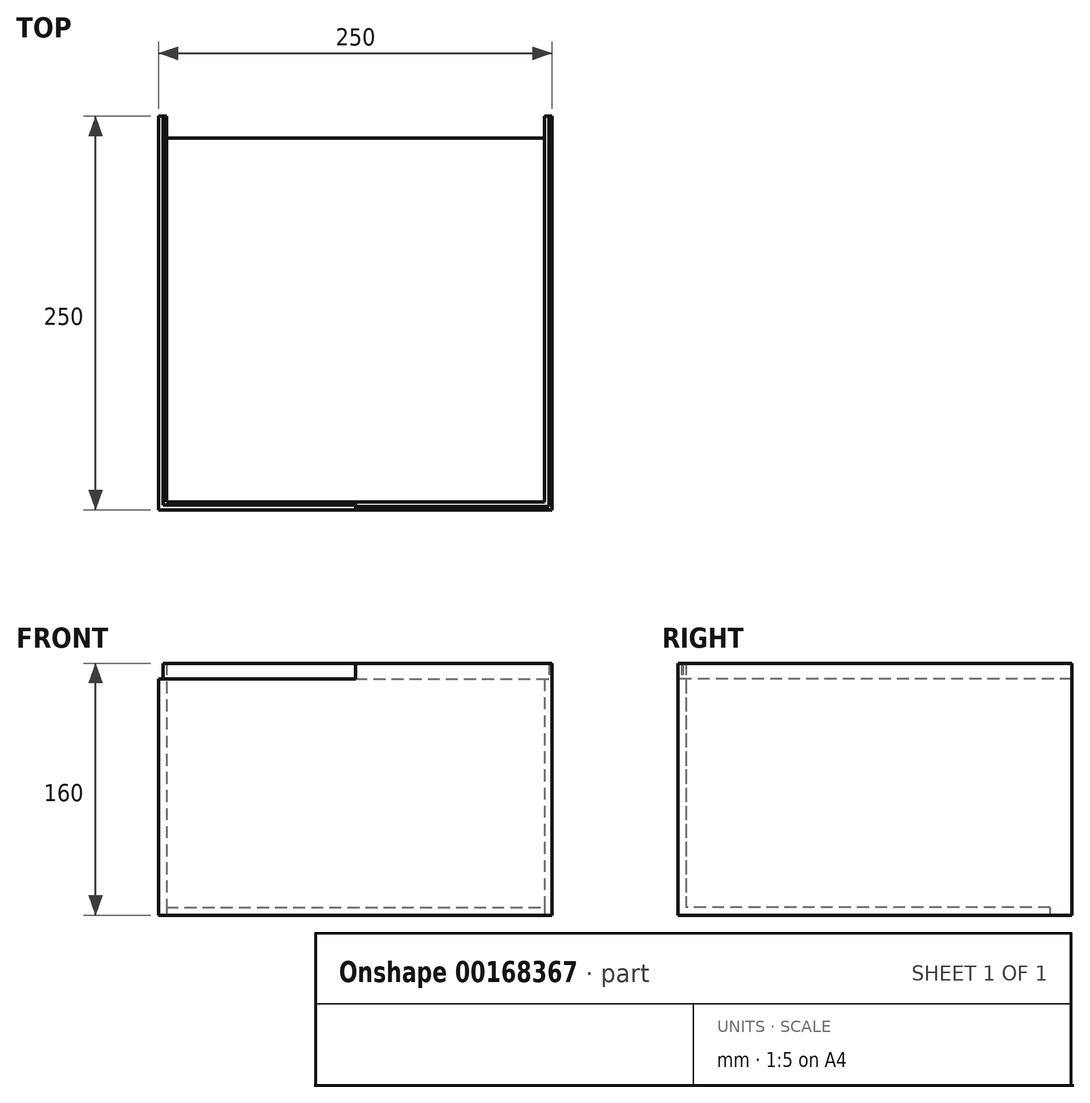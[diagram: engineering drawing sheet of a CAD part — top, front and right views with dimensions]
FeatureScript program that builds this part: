
annotation { "Feature Type Name" : "Feature", "Feature Type Description" : "" }
export const myFeature = defineFeature(function(context is Context, id is Id, definition is map)
    precondition{}
    {
        {
            var Q0;
            Q0=qCreatedBy(makeId("Top.planeOp"),FACE);
            var sketch = newSketch(context, id + "F0", { "sketchPlane" : qUnion([Q0])});
            skLineSegment(sketch, "E0.bottom", {"start": v(-131.9, 95.25) * mm, "end": v(-126.9, 95.25) * mm});
            skLineSegment(sketch, "E0.top", {"start": v(-131.9, -154.75) * mm, "end": v(118.1, -154.75) * mm});
            skLineSegment(sketch, "E0.left", {"start": v(-131.9, 95.25) * mm, "end": v(-131.9, -154.75) * mm});
            skLineSegment(sketch, "E0.right", {"start": v(118.1, 95.25) * mm, "end": v(118.1, -154.75) * mm});
            skLineSegment(sketch, "E1", {"start": v(113.1, 95.25) * mm, "end": v(118.1, 95.25) * mm});
            skLineSegment(sketch, "E2", {"start": v(-126.9, 95.25) * mm, "end": v(-126.9, 81.38) * mm});
            skLineSegment(sketch, "E3", {"start": v(-126.9, 81.38) * mm, "end": v(113.1, 81.38) * mm});
            skLineSegment(sketch, "E4", {"start": v(113.1, 81.38) * mm, "end": v(113.1, 95.25) * mm});
            skSolve(sketch);
        }
        {
            var Q0;
            Q0 = qSketchRegion(id + "F0", true);
            extrude(context, id + "F1", {"entities" : qUnion([Q0]), "depth" : 5 * mm});
        }
        {
            var Q0;
            Q0=makeQuery(id+"F1.opExtrude","CAP_FACE",FACE,{"disambiguationData":[OSD([sQuery(id+"F0.wireOp",EDGE,"E0.bottom"),sQuery(id+"F0.wireOp",EDGE,"E0.top"),sQuery(id+"F0.wireOp",EDGE,"E0.left"),sQuery(id+"F0.wireOp",EDGE,"E0.right"),sQuery(id+"F0.wireOp",EDGE,"E1"),sQuery(id+"F0.wireOp",EDGE,"E2"),sQuery(id+"F0.wireOp",EDGE,"E3"),sQuery(id+"F0.wireOp",EDGE,"E4")])],"isStart":false});
            var sketch = newSketch(context, id + "F2", { "sketchPlane" : qUnion([Q0])});
            skLineSegment(sketch, "E5.bottom", {"start": v(-126.9, 95.25) * mm, "end": v(-131.9, 95.25) * mm});
            skLineSegment(sketch, "E5.top", {"start": v(-126.9, -154.75) * mm, "end": v(-131.9, -154.75) * mm});
            skLineSegment(sketch, "E5.left", {"start": v(-126.9, 95.25) * mm, "end": v(-126.9, -154.75) * mm});
            skLineSegment(sketch, "E5.right", {"start": v(-131.9, 95.25) * mm, "end": v(-131.9, -154.75) * mm});
            skLineSegment(sketch, "E6.bottom", {"start": v(113.1, 95.25) * mm, "end": v(118.1, 95.25) * mm});
            skLineSegment(sketch, "E6.top", {"start": v(113.1, -154.75) * mm, "end": v(118.1, -154.75) * mm});
            skLineSegment(sketch, "E6.left", {"start": v(113.1, 95.25) * mm, "end": v(113.1, -154.75) * mm});
            skLineSegment(sketch, "E6.right", {"start": v(118.1, 95.25) * mm, "end": v(118.1, -154.75) * mm});
            skLineSegment(sketch, "E7.bottom", {"start": v(-126.9, -154.75) * mm, "end": v(113.1, -154.75) * mm});
            skLineSegment(sketch, "E7.top", {"start": v(-126.9, -149.75) * mm, "end": v(113.1, -149.75) * mm});
            skLineSegment(sketch, "E7.left", {"start": v(-126.9, -154.75) * mm, "end": v(-126.9, -149.75) * mm});
            skLineSegment(sketch, "E7.right", {"start": v(113.1, -154.75) * mm, "end": v(113.1, -149.75) * mm});
            skSolve(sketch);
        }
        {
            var Q0;
            Q0 = qSketchRegion(id + "F2", true);
            extrude(context, id + "F3", {"entities" : qUnion([Q0]), "operationType" : NewBodyOperationType.ADD, "depth" : 145 * mm});
        }
        {
            var Q0;
            Q0=makeQuery(id+"F3.opExtrude","CAP_FACE",FACE,{"disambiguationData":[OSD([sQuery(id+"F2.wireOp",EDGE,"E5.bottom"),sQuery(id+"F2.wireOp",EDGE,"E5.top"),sQuery(id+"F2.wireOp",EDGE,"E5.left"),sQuery(id+"F2.wireOp",EDGE,"E5.right"),sQuery(id+"F2.wireOp",EDGE,"E6.bottom"),sQuery(id+"F2.wireOp",EDGE,"E6.top"),sQuery(id+"F2.wireOp",EDGE,"E6.left"),sQuery(id+"F2.wireOp",EDGE,"E6.right"),sQuery(id+"F2.wireOp",EDGE,"E7.bottom"),sQuery(id+"F2.wireOp",EDGE,"E7.top")])],"isStart":false});
            var sketch = newSketch(context, id + "F4", { "sketchPlane" : qUnion([Q0])});
            skLineSegment(sketch, "E8.bottom", {"start": v(116.1, 95.25) * mm, "end": v(118.1, 95.25) * mm});
            skLineSegment(sketch, "E8.top", {"start": v(116.1, -152.75) * mm, "end": v(118.1, -154.75) * mm});
            skLineSegment(sketch, "E8.left", {"start": v(116.1, 95.25) * mm, "end": v(116.1, -152.75) * mm});
            skLineSegment(sketch, "E8.right", {"start": v(118.1, 95.25) * mm, "end": v(118.1, -154.75) * mm});
            skLineSegment(sketch, "E9", {"start": v(113.1, -149.75) * mm, "end": v(118.1, -154.75) * mm, "construction": true});
            skLineSegment(sketch, "E10.bottom", {"start": v(113.1, 95.25) * mm, "end": v(115.1, 95.25) * mm});
            skLineSegment(sketch, "E10.top", {"start": v(113.1, -149.75) * mm, "end": v(115.1, -151.75) * mm});
            skLineSegment(sketch, "E10.left", {"start": v(113.1, 95.25) * mm, "end": v(113.1, -149.75) * mm});
            skLineSegment(sketch, "E10.right", {"start": v(115.1, 95.25) * mm, "end": v(115.1, -151.75) * mm});
            skLineSegment(sketch, "E11.top", {"start": v(-129.9, -152.75) * mm, "end": v(116.1, -152.75) * mm});
            skLineSegment(sketch, "E11.left", {"start": v(-131.9, -154.75) * mm, "end": v(-129.9, -152.75) * mm});
            skLineSegment(sketch, "E12.bottom", {"start": v(-126.9, -149.75) * mm, "end": v(113.1, -149.75) * mm});
            skLineSegment(sketch, "E12.top", {"start": v(-128.9, -151.75) * mm, "end": v(115.1, -151.75) * mm});
            skLineSegment(sketch, "E12.left", {"start": v(-126.9, -149.75) * mm, "end": v(-128.9, -151.75) * mm});
            skLineSegment(sketch, "E13", {"start": v(-131.9, -154.75) * mm, "end": v(-126.9, -149.75) * mm, "construction": true});
            skLineSegment(sketch, "E14.bottom", {"start": v(-126.9, 95.25) * mm, "end": v(-128.9, 95.25) * mm});
            skLineSegment(sketch, "E14.left", {"start": v(-126.9, 95.25) * mm, "end": v(-126.9, -149.75) * mm});
            skLineSegment(sketch, "E14.right", {"start": v(-128.9, 95.25) * mm, "end": v(-128.9, -151.75) * mm});
            skLineSegment(sketch, "E15.bottom", {"start": v(-131.9, 95.25) * mm, "end": v(-129.9, 95.25) * mm});
            skLineSegment(sketch, "E15.left", {"start": v(-131.9, 95.25) * mm, "end": v(-131.9, -154.75) * mm});
            skLineSegment(sketch, "E15.right", {"start": v(-129.9, 95.25) * mm, "end": v(-129.9, -152.75) * mm});
            skLineSegment(sketch, "E16", {"start": v(-6.9, -149.75) * mm, "end": v(-6.9, -154.75) * mm});
            skSolve(sketch);
        }
        {
            var Q0;
            {var subQ0=sQuery(id+"F4.wireOp",EDGE,"E12.left");Q0=makeQuery(id+"F4.imprint","IMPRINT",FACE,{"disambiguationData":[TD([[makeQuery(id+"F4.imprint","IMPRINT",EDGE,{"derivedFrom":subQ0}),1.0]])]});}
            var Q1;
            Q1=makeQuery(id+"F4.imprint","IMPRINT",FACE,{"disambiguationData":[TD([[makeQuery(id+"F4.imprint","IMPRINT",EDGE,{"derivedFrom":sQuery(id+"F4.wireOp",EDGE,"E12.left")}),-1.0]])]});
            extrude(context, id + "F5", {"entities" : qUnion([Q0, Q1]), "operationType" : NewBodyOperationType.ADD, "depth" : 10 * mm});
        }
        {
            var Q0;
            Q0=makeQuery(id+"F4.imprint","IMPRINT",FACE,{"disambiguationData":[TD([[makeQuery(id+"F4.imprint","IMPRINT",EDGE,{"derivedFrom":sQuery(id+"F4.wireOp",EDGE,"E8.bottom")}),-1.0]])]});
            var Q1;
            {var subQ0=sQuery(id+"F4.wireOp",EDGE,"E8.top");Q1=makeQuery(id+"F4.imprint","IMPRINT",FACE,{"disambiguationData":[TD([[makeQuery(id+"F4.imprint","IMPRINT",EDGE,{"derivedFrom":subQ0}),-1.0]])]});}
            extrude(context, id + "F6", {"entities" : qUnion([Q0, Q1]), "operationType" : NewBodyOperationType.ADD, "depth" : 10 * mm});
        }
    });
